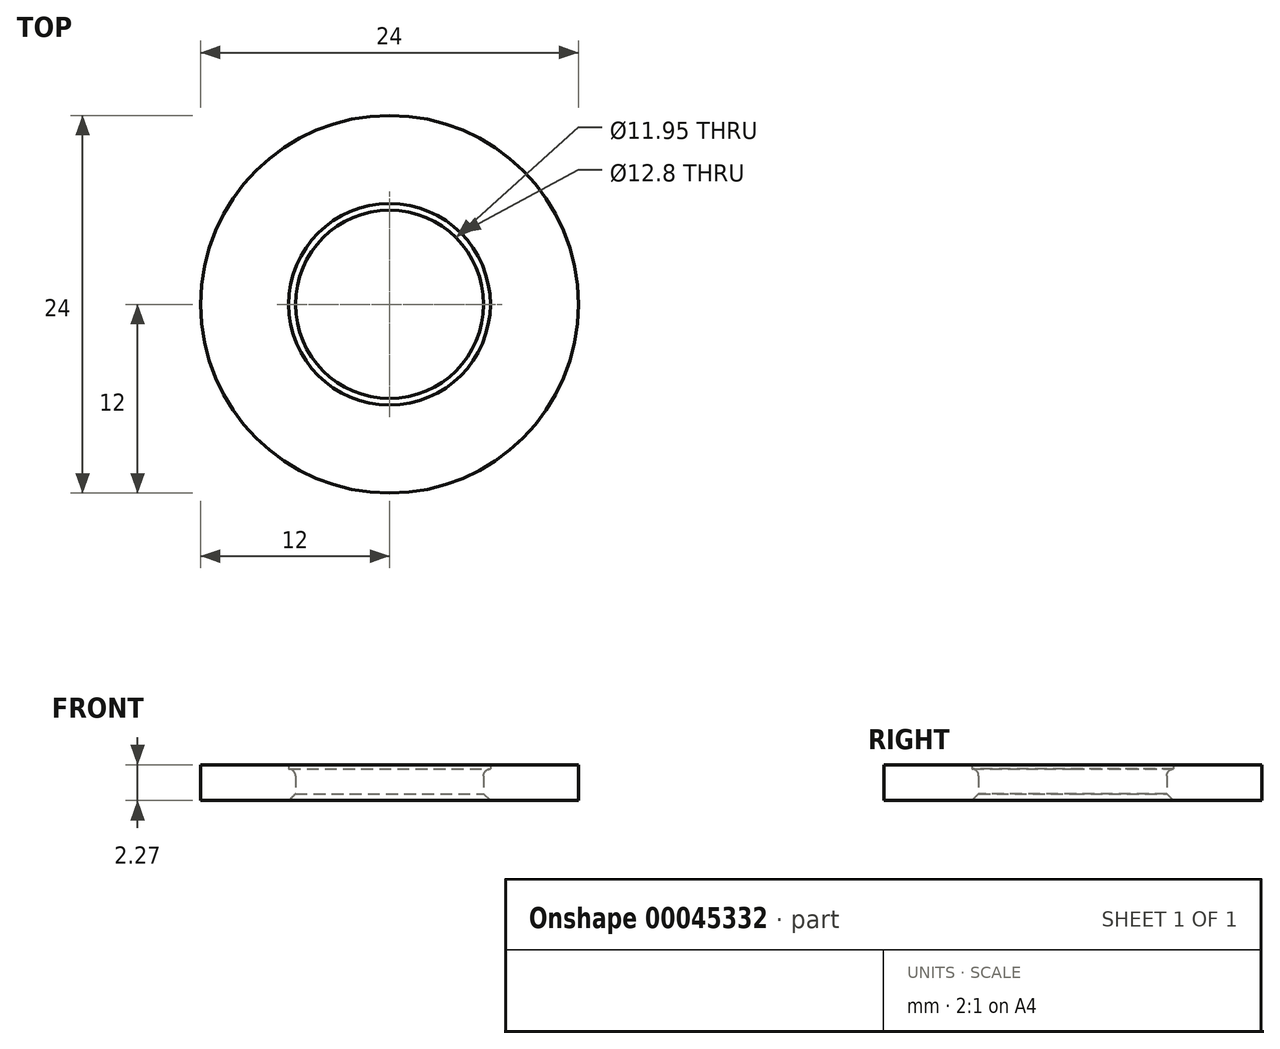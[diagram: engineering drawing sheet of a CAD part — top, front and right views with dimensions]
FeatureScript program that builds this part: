
annotation { "Feature Type Name" : "Feature", "Feature Type Description" : "" }
export const myFeature = defineFeature(function(context is Context, id is Id, definition is map)
    precondition{}
    {
        {
            var Q0;
            Q0=qCreatedBy(makeId("Right.planeOp"),FACE);
            var sketch = newSketch(context, id + "F0", { "sketchPlane" : qUnion([Q0])});
            skLineSegment(sketch, "E0.bottom", {"start": v(-6.4, 0) * mm, "end": v(-12, 0) * mm});
            skLineSegment(sketch, "E0.top", {"start": v(-6.4, 2.27) * mm, "end": v(-12, 2.27) * mm});
            skLineSegment(sketch, "E0.left", {"start": v(-6.4, 0) * mm, "end": v(-6.4, 2.27) * mm});
            skLineSegment(sketch, "E0.right", {"start": v(-12, 0) * mm, "end": v(-12, 2.27) * mm});
            skLineSegment(sketch, "E1", {"start": v(0, 0) * mm, "end": v(0, 36.12) * mm, "construction": true});
            skLineSegment(sketch, "E2.bottom", {"start": v(-6.4, 0) * mm, "end": v(-6.4, 0) * mm});
            skLineSegment(sketch, "E2.top", {"start": v(-6.4, 2) * mm, "end": v(-6.4, 2) * mm});
            skLineSegment(sketch, "E2.left", {"start": v(-6.4, 0) * mm, "end": v(-6.4, 2) * mm});
            skLineSegment(sketch, "E2.right", {"start": v(-5.97, 0.43) * mm, "end": v(-5.97, 1.57) * mm});
            skPoint(sketch, "E3.visualSharp", {"position": v(-5.97, 2) * mm});
            skArc(sketch, "E3.filletArc", {"start": v(-5.97, 1.57) * mm, "mid": v(-6.1, 1.88) * mm, "end": v(-6.4, 2) * mm});
            skPoint(sketch, "E4.visualSharp", {"position": v(-5.97, 0) * mm});
            skLineSegment(sketch, "E5", {"start": v(-5.97, 0.43) * mm, "end": v(-6.4, 0) * mm});
            skSolve(sketch);
        }
        {
            var Q0;
            Q0 = qSketchRegion(id + "F0", true);
            var Q1;
            Q1=sQuery(id+"F0.wireOp",EDGE,"E1");
            revolve(context, id + "F1", {"entities" : qUnion([Q0]), "axis" : qUnion([Q1]), "revolveType" : RevolveType.FULL});
        }
    });
